# Revit family: AF-W 71-80-90
name_source: partatom
category: HLS-Bauteile
revit_build: Autodesk Revit 2017 (Build: 20160720_1515(x64)
units: mm (PartAtom-declared; Revit-internal decimal feet)

## family parameters
Arbeitsebenenbasiert = Nein
Beim Laden mit Abzugskörper schneiden = Nein
Bemaßung runder Anschluss = Durchmesser verwenden
Gemeinsam genutzt = Nein
Immer vertikal = Ja
OmniClass-Nummer = 23.75.00.00
OmniClass-Titel = Climate Control (HVAC)
Raumberechnungspunkt = Nein
Teiletyp = Normal

## types (3) — shared parameters
Beschreibung = High efficiency air cooled
Condensation = Air
Depth = 262 mm  [stored 0.85958 ft]
Drain pipe = 16.5 mm  [stored 0.0541339 ft]
Gas = R410A
Gas pipe = 15.9 mm  [stored 0.0521654 ft]
Height = 343 mm  [stored 1.12533 ft]
Hersteller = Bosch
Installation = Indoor installation
Liquid pipe = 9.52 mm  [stored 0.0312336 ft]
Machine material = Galvanized Steel
Maximum Fuse Amps = 15 A
Min cable selection (power wiring) = 3×2.5 mm2
Minimum Circuit Amps = 1 A
Net Weight = 17.00 kg
Panel color = S1022
Power supply = 220-240V ~50/60Hz
Series = VRF
Width = 1194 mm

## per-type parameters (varying)
| type | Air Flow max | Cooling Capacity | Cooling Power Input | Heating Capacity | Heating Power Input |
| AF-W 90 | 1421.00 m³/h | 9 kW | 82 W | 10 kW | 82 W |
| AF-W 80 | 1195.00 m³/h | 8 kW | 53 W | 9 kW | 53 W |
| AF-W 71 | 1195.00 m³/h | 7 kW | 49 W | 8 kW | 49 W |

note: column(s) folded — value = type name in every type: Modell

note: [stored X ft] marks values corroborated as IEEE doubles in the binary element streams (Revit-internal decimal feet)
